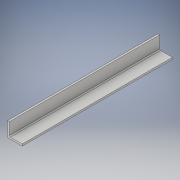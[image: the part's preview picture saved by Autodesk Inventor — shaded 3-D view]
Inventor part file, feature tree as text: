
AUTODESK INVENTOR PART (.ipt)
format: ipt  version: 2017 (Build 210142000, 142)  size: 99,328 bytes
history: native  units: in
note: dims shown in document units (in); Inventor stores cm internally (conversion verified against a paired STEP export)
features: extrude x1, sketch x1
ambient origin geometry x8: Origin, YZ Plane, XZ Plane, XY Plane, X Axis, Y Axis, Z Axis, Center Point
bodies: Solid1 (feature_tree)
feature tree (2):
  extrude  "Extrusion1"  Depth=1.0in
  sketch  "Sketch1"  dims[d4=10.188in d5=0.0in d6=1.0in d7=1.0in]
